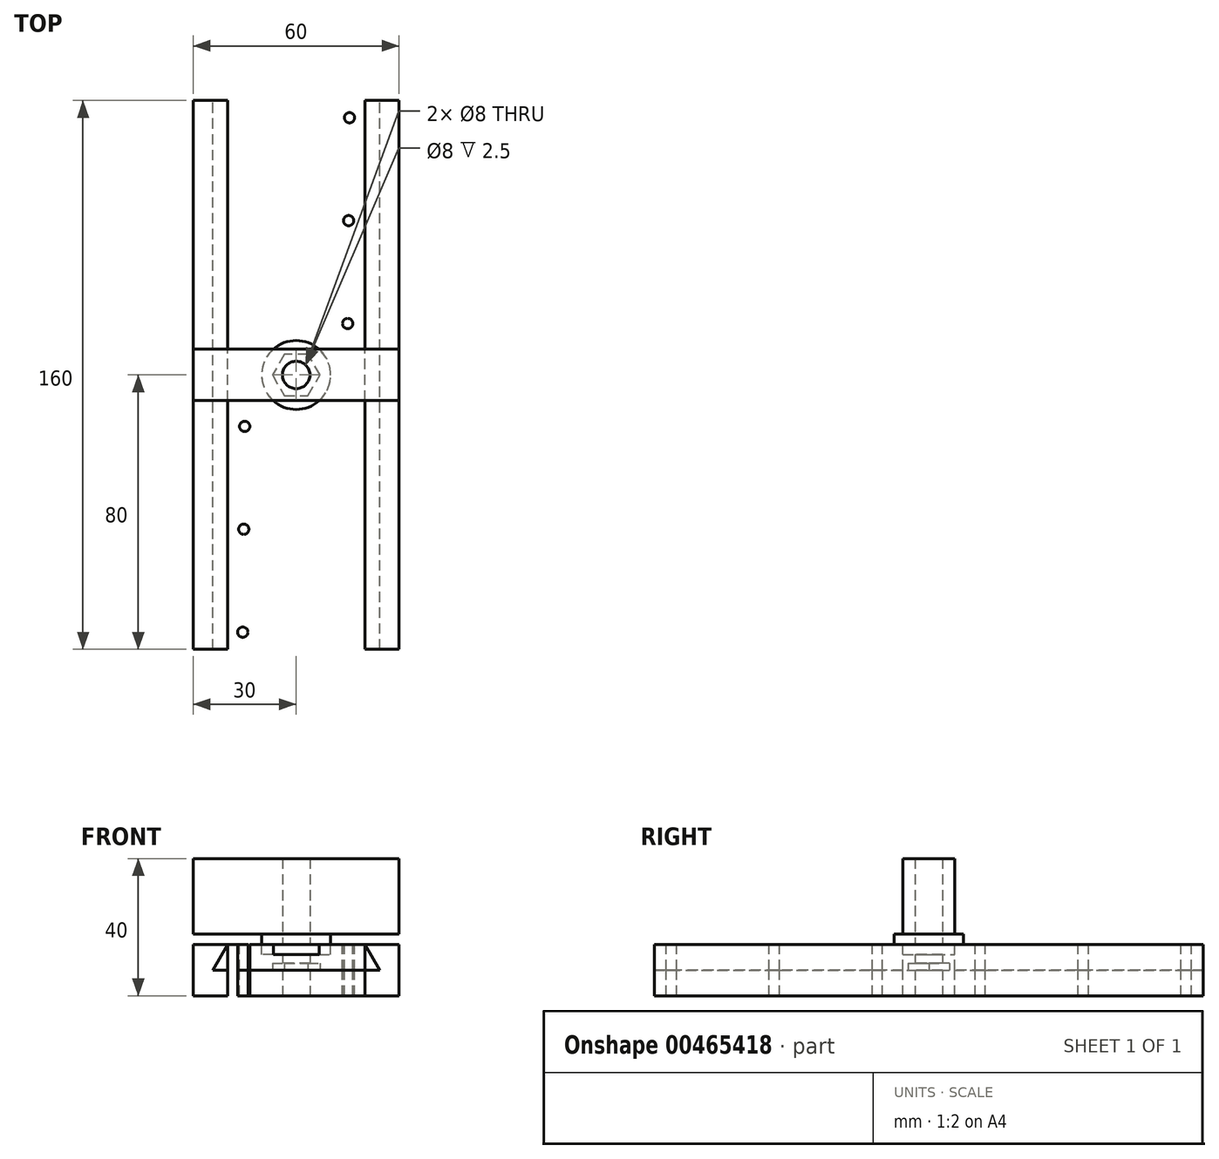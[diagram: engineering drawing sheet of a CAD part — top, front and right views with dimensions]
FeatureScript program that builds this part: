
annotation { "Feature Type Name" : "Feature", "Feature Type Description" : "" }
export const myFeature = defineFeature(function(context is Context, id is Id, definition is map)
    precondition{}
    {
        {
            assignVariable(context, id + "F0", {"name" : "Slider_len", "anyValue" : 80});
        }
        {
            var Q0;
            Q0=qCreatedBy(makeId("Front.planeOp"),FACE);
            var sketch = newSketch(context, id + "F1", { "sketchPlane" : qUnion([Q0])});
            skLineSegment(sketch, "E0.bottom", {"start": v(30, -7.5) * mm, "end": v(-30, -7.5) * mm});
            skLineSegment(sketch, "E0.top", {"start": v(30, 7.5) * mm, "end": v(-30, 7.5) * mm});
            skLineSegment(sketch, "E0.left", {"start": v(30, -7.5) * mm, "end": v(30, 7.5) * mm});
            skLineSegment(sketch, "E0.right", {"start": v(-30, -7.5) * mm, "end": v(-30, 7.5) * mm});
            skPoint(sketch, "E0.middle", {"position": v(0, 0) * mm});
            skLineSegment(sketch, "E1", {"start": v(20, 7.5) * mm, "end": v(24.33, 0) * mm});
            skLineSegment(sketch, "E2", {"start": v(24.33, 0) * mm, "end": v(0, 0) * mm});
            skLineSegment(sketch, "E3.MirrorCS", {"start": v(-20, 7.5) * mm, "end": v(-24.33, 0) * mm});
            skLineSegment(sketch, "E4.MirrorCS", {"start": v(-24.33, 0) * mm, "end": v(0, 0) * mm});
            skSolve(sketch);
        }
        {
            var Q0;
            Q0=makeQuery(id+"F1.imprint","IMPRINT",FACE,{"disambiguationData":[TD([[makeQuery(id+"F1.imprint","IMPRINT",EDGE,{"derivedFrom":sQuery(id+"F1.wireOp",EDGE,"E0.bottom")}),-1.0]])]});
            extrude(context, id + "F2", {"entities" : qUnion([Q0]), "depth" : (getVariable(context, 'Slider_len')) * mm, "hasSecondDirection" : true, "secondDirectionOppositeDirection" : true, "secondDirectionDepth" : (getVariable(context, 'Slider_len')) * mm});
        }
        {
            var Q0;
            {var subQ1=sQuery(id+"F1.wireOp",EDGE,"E1");Q0=makeQuery(id+"F1.imprint","IMPRINT",FACE,{"disambiguationData":[TD([[makeQuery(id+"F1.imprint","IMPRINT",EDGE,{"derivedFrom":subQ1}),-1.0]])]});}
            extrude(context, id + "F3", {"entities" : qUnion([Q0]), "depth" : (getVariable(context, 'Slider_len')) * mm, "hasSecondDirection" : true, "secondDirectionOppositeDirection" : true, "secondDirectionDepth" : (getVariable(context, 'Slider_len')) * mm});
        }
        {
            var Q0;
            Q0=makeQuery(id+"F3.opExtrude","SWEPT_FACE",FACE,{"disambiguationData":[OSD([sQuery(id+"F1.wireOp",EDGE,"E0.top")])]});
            var sketch = newSketch(context, id + "F4", { "sketchPlane" : qUnion([Q0])});
            skCircle(sketch, "E5", {"center": v(0, 0) * mm, "radius": 10.05 * mm});
            skLineSegment(sketch, "E6.bottom", {"start": v(30, -7.5) * mm, "end": v(-30, -7.5) * mm});
            skLineSegment(sketch, "E6.top", {"start": v(30, 7.5) * mm, "end": v(-30, 7.5) * mm});
            skLineSegment(sketch, "E6.left", {"start": v(30, -7.5) * mm, "end": v(30, 7.5) * mm});
            skLineSegment(sketch, "E6.right", {"start": v(-30, -7.5) * mm, "end": v(-30, 7.5) * mm});
            skCircle(sketch, "E7", {"center": v(0, 0) * mm, "radius": 4 * mm});
            skCircle(sketch, "E8", {"center": v(15, -15) * mm, "radius": 1.5 * mm});
            skCircle(sketch, "E9.MirrorC", {"center": v(-15, -15) * mm, "radius": 1.5 * mm});
            skCircle(sketch, "E10.0.1.0", {"center": v(15.27, -45) * mm, "radius": 1.5 * mm});
            skCircle(sketch, "E10.0.2.0", {"center": v(15.55, -75) * mm, "radius": 1.5 * mm});
            skLineSegment(sketch, "E10.direction1", {"start": v(15, -15) * mm, "end": v(40, -15) * mm, "construction": true});
            skLineSegment(sketch, "E10.direction2", {"start": v(15, -15) * mm, "end": v(15.27, -45) * mm, "construction": true});
            skCircle(sketch, "E11.MirrorC", {"center": v(-15.27, -45) * mm, "radius": 1.5 * mm});
            skCircle(sketch, "E12.MirrorC", {"center": v(-15.55, -75) * mm, "radius": 1.5 * mm});
            skCircle(sketch, "E13.MirrorC", {"center": v(15.55, 75) * mm, "radius": 1.5 * mm});
            skCircle(sketch, "E14.MirrorC", {"center": v(-15.55, 75) * mm, "radius": 1.5 * mm});
            skCircle(sketch, "E15.MirrorC", {"center": v(-15.27, 45) * mm, "radius": 1.5 * mm});
            skCircle(sketch, "E16.MirrorC", {"center": v(15.27, 45) * mm, "radius": 1.5 * mm});
            skCircle(sketch, "E17.MirrorC", {"center": v(-15, 15) * mm, "radius": 1.5 * mm});
            skCircle(sketch, "E18.MirrorC", {"center": v(15, 15) * mm, "radius": 1.5 * mm});
            skSolve(sketch);
        }
        {
            var Q0;
            Q0=makeQuery(id+"F4.imprint","IMPRINT",FACE,{"disambiguationData":[TD([[makeQuery(id+"F4.imprint","IMPRINT",EDGE,{"derivedFrom":sQuery(id+"F4.wireOp",EDGE,"E5")}),1.0]])]});
            var Q1;
            {var subQ0=sQuery(id+"F4.wireOp",EDGE,"E6.top");var subQ1=sQuery(id+"F4.wireOp",EDGE,"E5");var subQ2=makeQuery(id+"F4.imprint","INTERSECT",VERTEX,{"disambiguationData":[OD(0.0)],"derivedFrom":[subQ1,subQ0]});Q1=makeQuery(id+"F4.imprint","IMPRINT",FACE,{"disambiguationData":[TD([[makeQuery(id+"F4.imprint","IMPRINT",EDGE,{"disambiguationData":[TD([[subQ2,1.0]])],"derivedFrom":subQ1}),1.0]])]});}
            var Q2;
            {var subQ0=sQuery(id+"F4.wireOp",EDGE,"E6.bottom");var subQ1=sQuery(id+"F4.wireOp",EDGE,"E5");var subQ2=makeQuery(id+"F4.imprint","INTERSECT",VERTEX,{"disambiguationData":[OD(0.0)],"derivedFrom":[subQ1,subQ0]});Q2=makeQuery(id+"F4.imprint","IMPRINT",FACE,{"disambiguationData":[TD([[makeQuery(id+"F4.imprint","IMPRINT",EDGE,{"disambiguationData":[TD([[subQ2,-1.0]])],"derivedFrom":subQ1}),1.0]])]});}
            extrude(context, id + "F5", {"entities" : qUnion([Q0, Q1, Q2]), "operationType" : NewBodyOperationType.REMOVE, "oppositeDirection" : true, "depth" : 3 * mm});
        }
        {
            var Q0;
            {var subQ0=sQuery(id+"F4.wireOp",EDGE,"E6.right");Q0=makeQuery(id+"F4.imprint","IMPRINT",FACE,{"disambiguationData":[TD([[makeQuery(id+"F4.imprint","IMPRINT",EDGE,{"derivedFrom":subQ0}),-1.0]])]});}
            var Q1;
            {var subQ0=sQuery(id+"F4.wireOp",EDGE,"E6.top");var subQ1=sQuery(id+"F4.wireOp",EDGE,"E5");var subQ2=makeQuery(id+"F4.imprint","INTERSECT",VERTEX,{"disambiguationData":[OD(0.0)],"derivedFrom":[subQ1,subQ0]});Q1=makeQuery(id+"F4.imprint","IMPRINT",FACE,{"disambiguationData":[TD([[makeQuery(id+"F4.imprint","IMPRINT",EDGE,{"disambiguationData":[TD([[subQ2,-1.0]])],"derivedFrom":subQ1}),-1.0]])]});}
            var Q2;
            {var subQ0=sQuery(id+"F4.wireOp",EDGE,"E6.top");var subQ1=sQuery(id+"F4.wireOp",EDGE,"E5");var subQ2=makeQuery(id+"F4.imprint","INTERSECT",VERTEX,{"disambiguationData":[OD(0.0)],"derivedFrom":[subQ1,subQ0]});Q2=makeQuery(id+"F4.imprint","IMPRINT",FACE,{"disambiguationData":[TD([[makeQuery(id+"F4.imprint","IMPRINT",EDGE,{"disambiguationData":[TD([[subQ2,1.0]])],"derivedFrom":subQ1}),1.0]])]});}
            var Q3;
            {var subQ0=sQuery(id+"F4.wireOp",EDGE,"E6.bottom");var subQ1=sQuery(id+"F4.wireOp",EDGE,"E5");var subQ2=makeQuery(id+"F4.imprint","INTERSECT",VERTEX,{"disambiguationData":[OD(0.0)],"derivedFrom":[subQ1,subQ0]});Q3=makeQuery(id+"F4.imprint","IMPRINT",FACE,{"disambiguationData":[TD([[makeQuery(id+"F4.imprint","IMPRINT",EDGE,{"disambiguationData":[TD([[subQ2,-1.0]])],"derivedFrom":subQ1}),1.0]])]});}
            var Q4;
            {var subQ0=sQuery(id+"F4.wireOp",EDGE,"E6.top");var subQ1=sQuery(id+"F4.wireOp",EDGE,"E5");var subQ2=makeQuery(id+"F4.imprint","INTERSECT",VERTEX,{"disambiguationData":[OD(1.0)],"derivedFrom":[subQ1,subQ0]});Q4=makeQuery(id+"F4.imprint","IMPRINT",FACE,{"disambiguationData":[TD([[makeQuery(id+"F4.imprint","IMPRINT",EDGE,{"disambiguationData":[TD([[subQ2,1.0]])],"derivedFrom":subQ1}),-1.0]])]});}
            var Q5;
            {var subQ0=sQuery(id+"F4.wireOp",EDGE,"E6.top");var subQ1=sQuery(id+"F4.wireOp",EDGE,"E5");var subQ2=makeQuery(id+"F4.imprint","INTERSECT",VERTEX,{"disambiguationData":[OD(0.0)],"derivedFrom":[subQ1,subQ0]});Q5=makeQuery(id+"F4.imprint","IMPRINT",FACE,{"disambiguationData":[TD([[makeQuery(id+"F4.imprint","IMPRINT",EDGE,{"disambiguationData":[TD([[subQ2,-1.0]])],"derivedFrom":subQ1}),1.0]])]});}
            var Q6;
            {var subQ0=sQuery(id+"F4.wireOp",EDGE,"E6.left");Q6=makeQuery(id+"F4.imprint","IMPRINT",FACE,{"disambiguationData":[TD([[makeQuery(id+"F4.imprint","IMPRINT",EDGE,{"derivedFrom":subQ0}),1.0]])]});}
            extrude(context, id + "F6", {"entities" : qUnion([Q0, Q1, Q2, Q3, Q4, Q5, Q6]), "depth" : 25 * mm});
        }
        {
            var Q0;
            {var subQ0=sQuery(id+"F4.wireOp",EDGE,"E6.left");Q0=makeQuery(id+"F4.imprint","IMPRINT",FACE,{"disambiguationData":[TD([[makeQuery(id+"F4.imprint","IMPRINT",EDGE,{"derivedFrom":subQ0}),1.0]])]});}
            var Q1;
            {var subQ0=sQuery(id+"F4.wireOp",EDGE,"E6.top");var subQ1=sQuery(id+"F4.wireOp",EDGE,"E5");var subQ2=makeQuery(id+"F4.imprint","INTERSECT",VERTEX,{"disambiguationData":[OD(1.0)],"derivedFrom":[subQ1,subQ0]});Q1=makeQuery(id+"F4.imprint","IMPRINT",FACE,{"disambiguationData":[TD([[makeQuery(id+"F4.imprint","IMPRINT",EDGE,{"disambiguationData":[TD([[subQ2,1.0]])],"derivedFrom":subQ1}),-1.0]])]});}
            var Q2;
            {var subQ0=sQuery(id+"F4.wireOp",EDGE,"E6.top");var subQ1=sQuery(id+"F4.wireOp",EDGE,"E5");var subQ2=makeQuery(id+"F4.imprint","INTERSECT",VERTEX,{"disambiguationData":[OD(0.0)],"derivedFrom":[subQ1,subQ0]});Q2=makeQuery(id+"F4.imprint","IMPRINT",FACE,{"disambiguationData":[TD([[makeQuery(id+"F4.imprint","IMPRINT",EDGE,{"disambiguationData":[TD([[subQ2,-1.0]])],"derivedFrom":subQ1}),-1.0]])]});}
            var Q3;
            {var subQ0=sQuery(id+"F4.wireOp",EDGE,"E6.right");Q3=makeQuery(id+"F4.imprint","IMPRINT",FACE,{"disambiguationData":[TD([[makeQuery(id+"F4.imprint","IMPRINT",EDGE,{"derivedFrom":subQ0}),-1.0]])]});}
            extrude(context, id + "F7", {"entities" : qUnion([Q0, Q1, Q2, Q3]), "operationType" : NewBodyOperationType.REMOVE, "depth" : 3 * mm});
        }
        {
            var Q0;
            Q0=makeQuery(id+"F4.imprint","IMPRINT",FACE,{"disambiguationData":[TD([[makeQuery(id+"F4.imprint","IMPRINT",EDGE,{"derivedFrom":sQuery(id+"F4.wireOp",EDGE,"E7")}),1.0]])]});
            var Q1;
            {var subQ0=sQuery(id+"F4.wireOp",EDGE,"E6.top");var subQ1=sQuery(id+"F4.wireOp",EDGE,"E5");var subQ2=makeQuery(id+"F4.imprint","INTERSECT",VERTEX,{"disambiguationData":[OD(0.0)],"derivedFrom":[subQ1,subQ0]});Q1=makeQuery(id+"F4.imprint","IMPRINT",FACE,{"disambiguationData":[TD([[makeQuery(id+"F4.imprint","IMPRINT",EDGE,{"disambiguationData":[TD([[subQ2,1.0]])],"derivedFrom":subQ1}),1.0]])]});}
            var Q2;
            {var subQ0=sQuery(id+"F4.wireOp",EDGE,"E6.bottom");var subQ1=sQuery(id+"F4.wireOp",EDGE,"E5");var subQ2=makeQuery(id+"F4.imprint","INTERSECT",VERTEX,{"disambiguationData":[OD(0.0)],"derivedFrom":[subQ1,subQ0]});Q2=makeQuery(id+"F4.imprint","IMPRINT",FACE,{"disambiguationData":[TD([[makeQuery(id+"F4.imprint","IMPRINT",EDGE,{"disambiguationData":[TD([[subQ2,-1.0]])],"derivedFrom":subQ1}),1.0]])]});}
            extrude(context, id + "F8", {"entities" : qUnion([Q0, Q1, Q2]), "operationType" : NewBodyOperationType.REMOVE, "endBound" : BoundingType.THROUGH_ALL, "depth" : 25 * mm, "hasSecondDirection" : true, "secondDirectionBound" : SecondDirectionBoundingType.THROUGH_ALL, "secondDirectionOppositeDirection" : true, "secondDirectionDepth" : 25 * mm});
        }
        {
            var Q0;
            {var subQ0=sQuery(id+"F4.wireOp",EDGE,"E6.top");var subQ1=sQuery(id+"F4.wireOp",EDGE,"E5");var subQ2=makeQuery(id+"F4.imprint","INTERSECT",VERTEX,{"disambiguationData":[OD(0.0)],"derivedFrom":[subQ1,subQ0]});Q0=makeQuery(id+"F4.imprint","IMPRINT",FACE,{"disambiguationData":[TD([[makeQuery(id+"F4.imprint","IMPRINT",EDGE,{"disambiguationData":[TD([[subQ2,1.0]])],"derivedFrom":subQ1}),1.0]])]});}
            var Q1;
            {var subQ0=sQuery(id+"F4.wireOp",EDGE,"E6.bottom");var subQ1=sQuery(id+"F4.wireOp",EDGE,"E5");var subQ2=makeQuery(id+"F4.imprint","INTERSECT",VERTEX,{"disambiguationData":[OD(0.0)],"derivedFrom":[subQ1,subQ0]});Q1=makeQuery(id+"F4.imprint","IMPRINT",FACE,{"disambiguationData":[TD([[makeQuery(id+"F4.imprint","IMPRINT",EDGE,{"disambiguationData":[TD([[subQ2,-1.0]])],"derivedFrom":subQ1}),1.0]])]});}
            extrude(context, id + "F9", {"entities" : qUnion([Q0, Q1]), "operationType" : NewBodyOperationType.ADD, "depth" : 3 * mm});
        }
        {
            var Q0;
            Q0=makeQuery(id+"F3.opExtrude","SWEPT_FACE",FACE,{"disambiguationData":[OSD([sQuery(id+"F1.wireOp",EDGE,"E2"),sQuery(id+"F1.wireOp",EDGE,"E4.MirrorCS")])]});
            var sketch = newSketch(context, id + "F10", { "sketchPlane" : qUnion([Q0])});
            skCircle(sketch, "E19.cCircle", {"center": v(0, 0) * mm, "radius": 6 * mm, "construction": true});
            skLineSegment(sketch, "E19.0", {"start": v(3.46, 6) * mm, "end": v(6.93, 0) * mm});
            skLineSegment(sketch, "E19.1", {"start": v(6.93, 0) * mm, "end": v(3.46, -6) * mm});
            skLineSegment(sketch, "E19.2", {"start": v(3.46, -6) * mm, "end": v(-3.46, -6) * mm});
            skLineSegment(sketch, "E19.3", {"start": v(-3.46, -6) * mm, "end": v(-6.93, 0) * mm});
            skLineSegment(sketch, "E19.4", {"start": v(-6.93, 0) * mm, "end": v(-3.46, 6) * mm});
            skLineSegment(sketch, "E19.5", {"start": v(-3.46, 6) * mm, "end": v(3.46, 6) * mm});
            skPoint(sketch, "E19.0.midPoint", {"position": v(5.2, 3) * mm});
            skSolve(sketch);
        }
        {
            var Q0;
            Q0=makeQuery(id+"F10.imprint","IMPRINT",FACE,{"disambiguationData":[TD([[makeQuery(id+"F10.imprint","IMPRINT",EDGE,{"derivedFrom":sQuery(id+"F10.wireOp",EDGE,"E19.0")}),-1.0]])]});
            extrude(context, id + "F11", {"entities" : qUnion([Q0]), "operationType" : NewBodyOperationType.REMOVE, "oppositeDirection" : true, "depth" : 2 * mm});
        }
        {
            var Q0;
            Q0=makeQuery(id+"F4.imprint","IMPRINT",FACE,{"disambiguationData":[TD([[makeQuery(id+"F4.imprint","IMPRINT",EDGE,{"derivedFrom":sQuery(id+"F4.wireOp",EDGE,"E7")}),1.0]])]});
            extrude(context, id + "F12", {"entities" : qUnion([Q0]), "operationType" : NewBodyOperationType.REMOVE, "endBound" : BoundingType.THROUGH_ALL, "oppositeDirection" : true, "depth" : 25 * mm});
        }
        {
            var Q0;
            Q0=makeQuery(id+"F4.imprint","IMPRINT",FACE,{"disambiguationData":[TD([[makeQuery(id+"F4.imprint","IMPRINT",EDGE,{"derivedFrom":sQuery(id+"F4.wireOp",EDGE,"E18.MirrorC")}),-1.0]])]});
            var Q1;
            Q1=makeQuery(id+"F4.imprint","IMPRINT",FACE,{"disambiguationData":[TD([[makeQuery(id+"F4.imprint","IMPRINT",EDGE,{"derivedFrom":sQuery(id+"F4.wireOp",EDGE,"E16.MirrorC")}),-1.0]])]});
            var Q2;
            Q2=makeQuery(id+"F4.imprint","IMPRINT",FACE,{"disambiguationData":[TD([[makeQuery(id+"F4.imprint","IMPRINT",EDGE,{"derivedFrom":sQuery(id+"F4.wireOp",EDGE,"E15.MirrorC")}),1.0]])]});
            var Q3;
            Q3=makeQuery(id+"F4.imprint","IMPRINT",FACE,{"disambiguationData":[TD([[makeQuery(id+"F4.imprint","IMPRINT",EDGE,{"derivedFrom":sQuery(id+"F4.wireOp",EDGE,"E17.MirrorC")}),1.0]])]});
            var Q4;
            Q4=makeQuery(id+"F4.imprint","IMPRINT",FACE,{"disambiguationData":[TD([[makeQuery(id+"F4.imprint","IMPRINT",EDGE,{"derivedFrom":sQuery(id+"F4.wireOp",EDGE,"E9.MirrorC")}),-1.0]])]});
            var Q5;
            Q5=makeQuery(id+"F4.imprint","IMPRINT",FACE,{"disambiguationData":[TD([[makeQuery(id+"F4.imprint","IMPRINT",EDGE,{"derivedFrom":sQuery(id+"F4.wireOp",EDGE,"E8")}),1.0]])]});
            var Q6;
            Q6=makeQuery(id+"F4.imprint","IMPRINT",FACE,{"disambiguationData":[TD([[makeQuery(id+"F4.imprint","IMPRINT",EDGE,{"derivedFrom":sQuery(id+"F4.wireOp",EDGE,"E10.0.1.0")}),1.0]])]});
            var Q7;
            Q7=makeQuery(id+"F4.imprint","IMPRINT",FACE,{"disambiguationData":[TD([[makeQuery(id+"F4.imprint","IMPRINT",EDGE,{"derivedFrom":sQuery(id+"F4.wireOp",EDGE,"E11.MirrorC")}),-1.0]])]});
            var Q8;
            Q8=makeQuery(id+"F4.imprint","IMPRINT",FACE,{"disambiguationData":[TD([[makeQuery(id+"F4.imprint","IMPRINT",EDGE,{"derivedFrom":sQuery(id+"F4.wireOp",EDGE,"E12.MirrorC")}),-1.0]])]});
            var Q9;
            Q9=makeQuery(id+"F4.imprint","IMPRINT",FACE,{"disambiguationData":[TD([[makeQuery(id+"F4.imprint","IMPRINT",EDGE,{"derivedFrom":sQuery(id+"F4.wireOp",EDGE,"E10.0.2.0")}),1.0]])]});
            var Q10;
            Q10=makeQuery(id+"F4.imprint","IMPRINT",FACE,{"disambiguationData":[TD([[makeQuery(id+"F4.imprint","IMPRINT",EDGE,{"derivedFrom":sQuery(id+"F4.wireOp",EDGE,"E13.MirrorC")}),-1.0]])]});
            var Q11;
            Q11=makeQuery(id+"F4.imprint","IMPRINT",FACE,{"disambiguationData":[TD([[makeQuery(id+"F4.imprint","IMPRINT",EDGE,{"derivedFrom":sQuery(id+"F4.wireOp",EDGE,"E14.MirrorC")}),1.0]])]});
            extrude(context, id + "F13", {"entities" : qUnion([Q0, Q1, Q2, Q3, Q4, Q5, Q6, Q7, Q8, Q9, Q10, Q11]), "operationType" : NewBodyOperationType.REMOVE, "endBound" : BoundingType.THROUGH_ALL, "oppositeDirection" : true, "depth" : 25 * mm});
        }
    });
